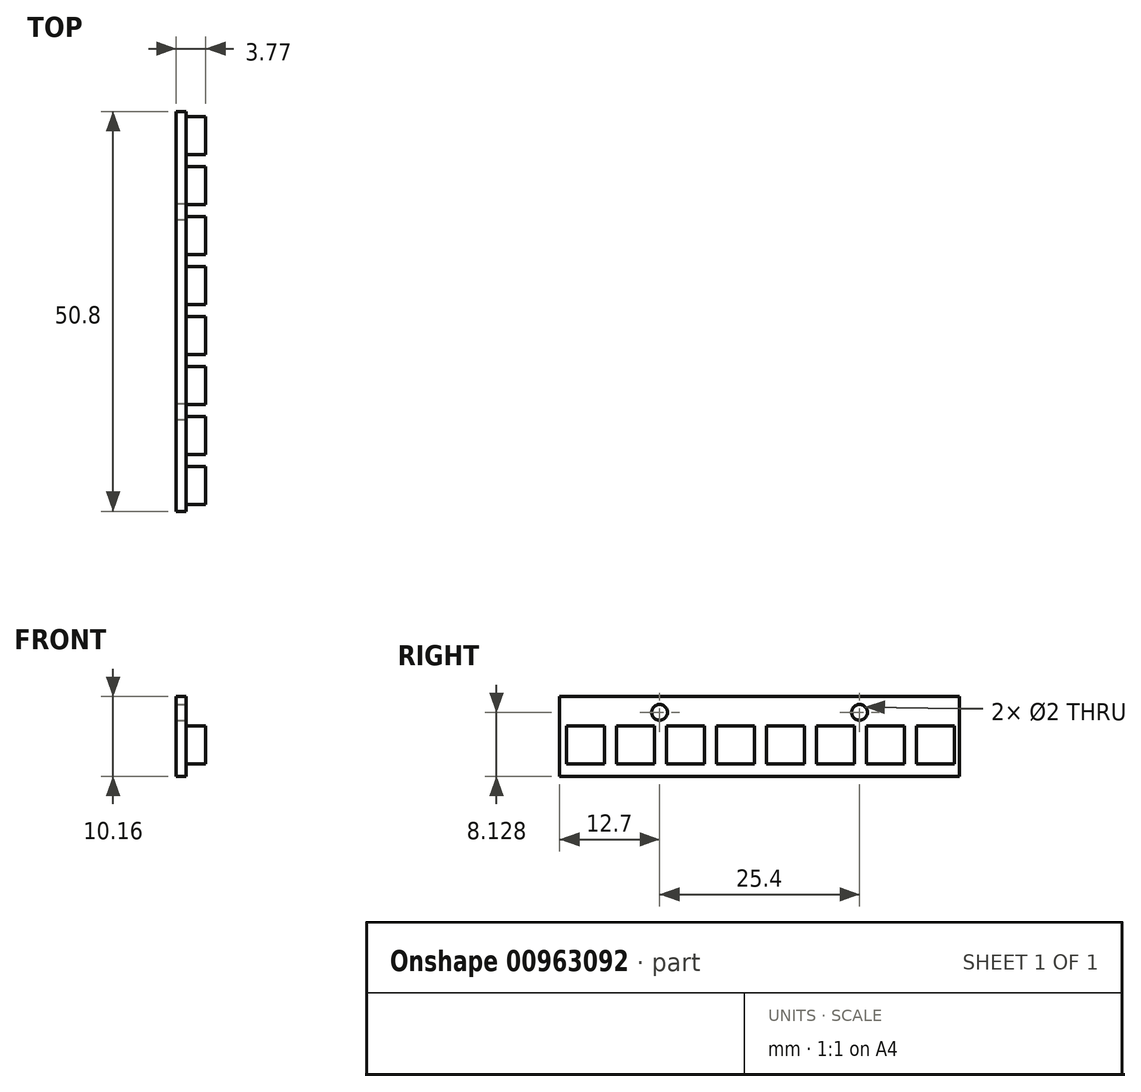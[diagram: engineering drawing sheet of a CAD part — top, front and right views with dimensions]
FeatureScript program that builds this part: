
annotation { "Feature Type Name" : "Feature", "Feature Type Description" : "" }
export const myFeature = defineFeature(function(context is Context, id is Id, definition is map)
    precondition{}
    {
        {
            var Q0;
            Q0=qCreatedBy(makeId("Right.planeOp"),FACE);
            var sketch = newSketch(context, id + "F0", { "sketchPlane" : qUnion([Q0])});
            skLineSegment(sketch, "E0.bottom", {"start": v(-25.4, 5.08) * mm, "end": v(25.4, 5.08) * mm});
            skLineSegment(sketch, "E0.top", {"start": v(-25.4, -5.08) * mm, "end": v(25.4, -5.08) * mm});
            skLineSegment(sketch, "E0.left", {"start": v(-25.4, 5.08) * mm, "end": v(-25.4, -5.08) * mm});
            skLineSegment(sketch, "E0.right", {"start": v(25.4, 5.08) * mm, "end": v(25.4, -5.08) * mm});
            skLineSegment(sketch, "E1", {"start": v(-25.4, 5.08) * mm, "end": v(25.4, -5.08) * mm, "construction": true});
            skCircle(sketch, "E2", {"center": v(-12.7, 3.05) * mm, "radius": 1 * mm});
            skCircle(sketch, "E3", {"center": v(12.7, 3.05) * mm, "radius": 1 * mm});
            skSolve(sketch);
        }
        {
            var Q0;
            Q0 = qSketchRegion(id + "F0", true);
            extrude(context, id + "F1", {"entities" : qUnion([Q0]), "oppositeDirection" : true, "depth" : (2.54 / 2) * mm, "offsetDistance" : 25 * mm});
        }
        {
            var Q0;
            Q0=makeQuery(id+"F1.opExtrude","CAP_FACE",FACE,{"disambiguationData":[OSD([sQuery(id+"F0.wireOp",EDGE,"E0.bottom"),sQuery(id+"F0.wireOp",EDGE,"E0.top"),sQuery(id+"F0.wireOp",EDGE,"E0.left"),sQuery(id+"F0.wireOp",EDGE,"E0.right"),sQuery(id+"F0.wireOp",EDGE,"E2"),sQuery(id+"F0.wireOp",EDGE,"E3")])],"isStart":true});
            var sketch = newSketch(context, id + "F2", { "sketchPlane" : qUnion([Q0])});
            skLineSegment(sketch, "E4.bottom", {"start": v(-24.5, 1.32) * mm, "end": v(-19.7, 1.32) * mm});
            skLineSegment(sketch, "E4.top", {"start": v(-24.5, -3.48) * mm, "end": v(-19.7, -3.48) * mm});
            skLineSegment(sketch, "E4.left", {"start": v(-24.5, 1.32) * mm, "end": v(-24.5, -3.48) * mm});
            skLineSegment(sketch, "E4.right", {"start": v(-19.7, 1.32) * mm, "end": v(-19.7, -3.48) * mm});
            skLineSegment(sketch, "E5.bottom", {"start": v(-18.15, 1.32) * mm, "end": v(-13.35, 1.32) * mm});
            skLineSegment(sketch, "E5.top", {"start": v(-18.15, -3.48) * mm, "end": v(-13.35, -3.48) * mm});
            skLineSegment(sketch, "E5.left", {"start": v(-18.15, 1.32) * mm, "end": v(-18.15, -3.48) * mm});
            skLineSegment(sketch, "E5.right", {"start": v(-13.35, 1.32) * mm, "end": v(-13.35, -3.48) * mm});
            skLineSegment(sketch, "E6.bottom", {"start": v(-11.8, 1.32) * mm, "end": v(-7, 1.32) * mm});
            skLineSegment(sketch, "E6.top", {"start": v(-11.8, -3.48) * mm, "end": v(-7, -3.48) * mm});
            skLineSegment(sketch, "E6.left", {"start": v(-11.8, 1.32) * mm, "end": v(-11.8, -3.48) * mm});
            skLineSegment(sketch, "E6.right", {"start": v(-7, 1.32) * mm, "end": v(-7, -3.48) * mm});
            skLineSegment(sketch, "E7.bottom", {"start": v(-5.45, 1.32) * mm, "end": v(-0.65, 1.32) * mm});
            skLineSegment(sketch, "E7.top", {"start": v(-5.45, -3.48) * mm, "end": v(-0.65, -3.48) * mm});
            skLineSegment(sketch, "E7.left", {"start": v(-5.45, 1.32) * mm, "end": v(-5.45, -3.48) * mm});
            skLineSegment(sketch, "E7.right", {"start": v(-0.65, 1.32) * mm, "end": v(-0.65, -3.48) * mm});
            skLineSegment(sketch, "E8.bottom", {"start": v(0.9, 1.32) * mm, "end": v(5.7, 1.32) * mm});
            skLineSegment(sketch, "E8.top", {"start": v(0.9, -3.48) * mm, "end": v(5.7, -3.48) * mm});
            skLineSegment(sketch, "E8.left", {"start": v(0.9, 1.32) * mm, "end": v(0.9, -3.48) * mm});
            skLineSegment(sketch, "E8.right", {"start": v(5.7, 1.32) * mm, "end": v(5.7, -3.48) * mm});
            skLineSegment(sketch, "E9.bottom", {"start": v(7.25, 1.32) * mm, "end": v(12.05, 1.32) * mm});
            skLineSegment(sketch, "E9.top", {"start": v(7.25, -3.48) * mm, "end": v(12.05, -3.48) * mm});
            skLineSegment(sketch, "E9.left", {"start": v(7.25, 1.32) * mm, "end": v(7.25, -3.48) * mm});
            skLineSegment(sketch, "E9.right", {"start": v(12.05, 1.32) * mm, "end": v(12.05, -3.48) * mm});
            skLineSegment(sketch, "E10.bottom", {"start": v(13.6, 1.32) * mm, "end": v(18.4, 1.32) * mm});
            skLineSegment(sketch, "E10.top", {"start": v(13.6, -3.48) * mm, "end": v(18.4, -3.48) * mm});
            skLineSegment(sketch, "E10.left", {"start": v(13.6, 1.32) * mm, "end": v(13.6, -3.48) * mm});
            skLineSegment(sketch, "E10.right", {"start": v(18.4, 1.32) * mm, "end": v(18.4, -3.48) * mm});
            skLineSegment(sketch, "E11.bottom", {"start": v(19.95, 1.32) * mm, "end": v(24.75, 1.32) * mm});
            skLineSegment(sketch, "E11.top", {"start": v(19.95, -3.48) * mm, "end": v(24.75, -3.48) * mm});
            skLineSegment(sketch, "E11.left", {"start": v(19.95, 1.32) * mm, "end": v(19.95, -3.48) * mm});
            skLineSegment(sketch, "E11.right", {"start": v(24.75, 1.32) * mm, "end": v(24.75, -3.48) * mm});
            skLineSegment(sketch, "E12", {"start": v(-24.5, 1.32) * mm, "end": v(-19.7, -3.48) * mm, "construction": true});
            skPoint(sketch, "E13", {"position": v(-22.1, -1.08) * mm});
            skLineSegment(sketch, "E14", {"start": v(-24.5, -1.08) * mm, "end": v(-18.15, -1.08) * mm, "construction": true});
            skLineSegment(sketch, "E15", {"start": v(-18.15, -1.08) * mm, "end": v(-11.8, -1.08) * mm, "construction": true});
            skLineSegment(sketch, "E16", {"start": v(-11.8, -1.08) * mm, "end": v(-5.45, -1.08) * mm, "construction": true});
            skLineSegment(sketch, "E17", {"start": v(-5.45, -1.08) * mm, "end": v(0.9, -1.08) * mm, "construction": true});
            skLineSegment(sketch, "E18", {"start": v(0.9, -1.08) * mm, "end": v(7.25, -1.08) * mm, "construction": true});
            skLineSegment(sketch, "E19", {"start": v(7.25, -1.08) * mm, "end": v(13.6, -1.08) * mm, "construction": true});
            skLineSegment(sketch, "E20", {"start": v(13.6, -1.08) * mm, "end": v(19.95, -1.08) * mm, "construction": true});
            skLineSegment(sketch, "E21", {"start": v(0, 0) * mm, "end": v(0, 6.69) * mm, "construction": true});
            skSolve(sketch);
        }
        {
            var Q0;
            Q0 = qSketchRegion(id + "F2", true);
            extrude(context, id + "F3", {"entities" : qUnion([Q0]), "operationType" : NewBodyOperationType.ADD, "depth" : 2.5 * mm, "offsetDistance" : 25 * mm});
        }
    });
